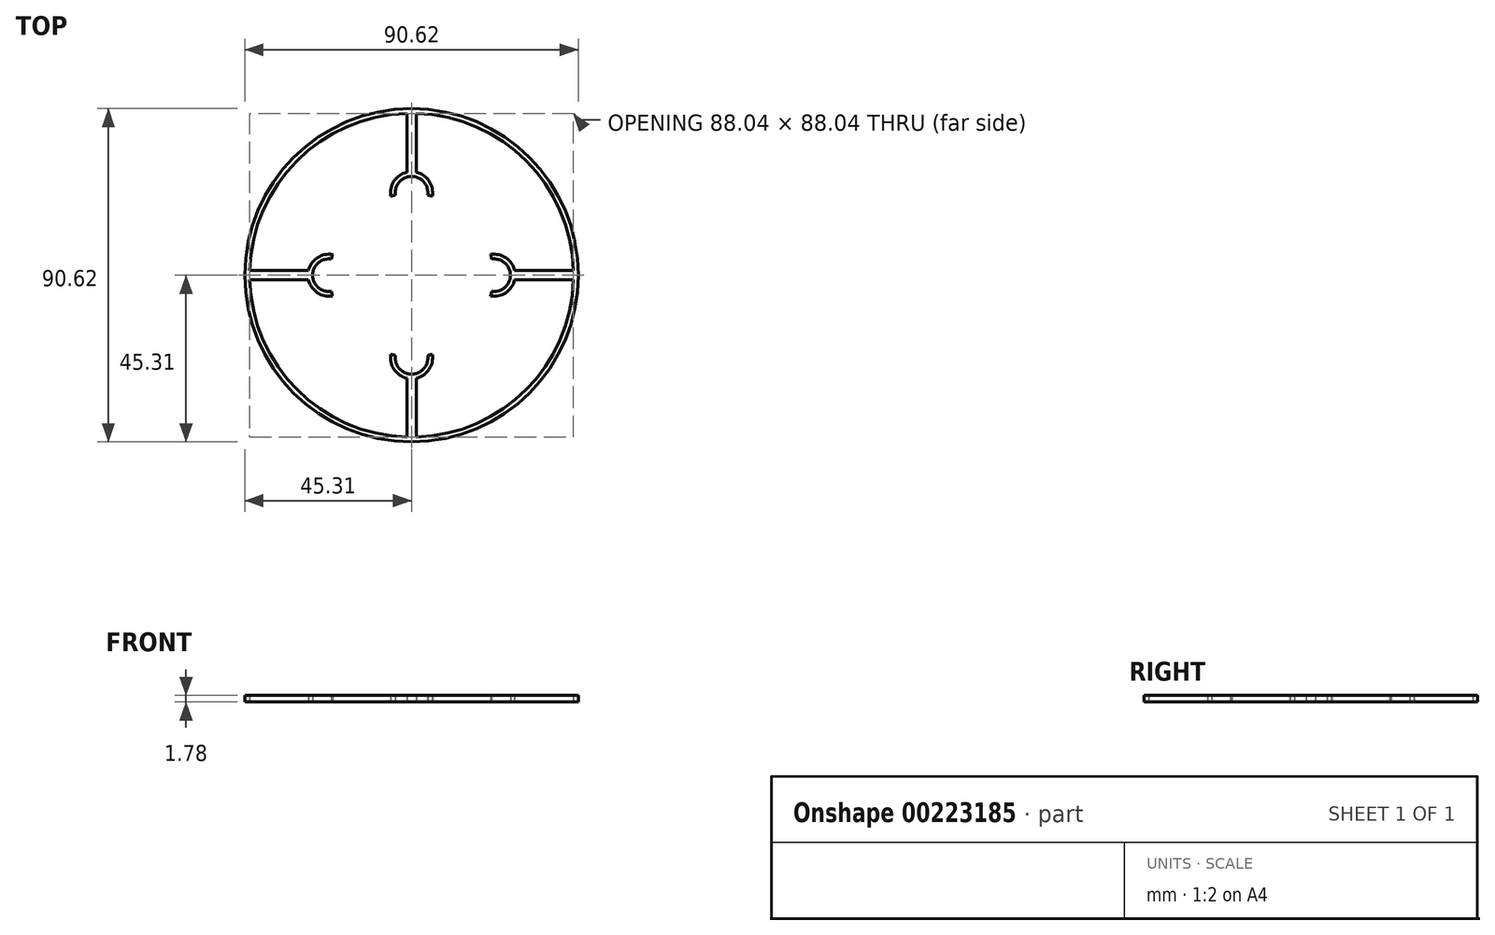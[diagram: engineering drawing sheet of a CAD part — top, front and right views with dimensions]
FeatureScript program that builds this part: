
annotation { "Feature Type Name" : "Feature", "Feature Type Description" : "" }
export const myFeature = defineFeature(function(context is Context, id is Id, definition is map)
    precondition{}
    {
        {
            var Q0;
            Q0=qCreatedBy(makeId("Top.planeOp"),FACE);
            var sketch = newSketch(context, id + "F0", { "sketchPlane" : qUnion([Q0])});
            skCircle(sketch, "E0", {"center": v(0, 22.45) * mm, "radius": 4.45 * mm});
            skCircle(sketch, "E1", {"center": v(22.45, 0) * mm, "radius": 4.45 * mm});
            skCircle(sketch, "E2", {"center": v(0, -22.45) * mm, "radius": 4.45 * mm});
            skCircle(sketch, "E3", {"center": v(-22.45, 0) * mm, "radius": 4.45 * mm});
            skLineSegment(sketch, "E4", {"start": v(0, 22.45) * mm, "end": v(0, 0) * mm, "construction": true});
            skLineSegment(sketch, "E5", {"start": v(0, 0) * mm, "end": v(22.45, 0) * mm, "construction": true});
            skLineSegment(sketch, "E6", {"start": v(-22.45, 0) * mm, "end": v(0, 0) * mm, "construction": true});
            skLineSegment(sketch, "E7", {"start": v(0, 0) * mm, "end": v(0, -22.45) * mm, "construction": true});
            skArc(sketch, "E8.0", {"start": v(-1.27, 28.02) * mm, "mid": v(0, 16.74) * mm, "end": v(1.27, 28.02) * mm});
            skArc(sketch, "E9.0", {"start": v(-28.02, -1.27) * mm, "mid": v(-16.74, 0) * mm, "end": v(-28.02, 1.27) * mm});
            skArc(sketch, "E10.0", {"start": v(28.02, 1.27) * mm, "mid": v(16.74, 0) * mm, "end": v(28.02, -1.27) * mm});
            skArc(sketch, "E11.0", {"start": v(1.27, -28.02) * mm, "mid": v(0, -16.74) * mm, "end": v(-1.27, -28.02) * mm});
            skLineSegment(sketch, "E12", {"start": v(0, 22.45) * mm, "end": v(0, 44.04) * mm, "construction": true});
            skArc(sketch, "E13", {"start": v(-1.27, 44.02) * mm, "mid": v(-31.14, 31.14) * mm, "end": v(-44.02, 1.27) * mm});
            skCircle(sketch, "E14.0", {"center": v(0, 0) * mm, "radius": 45.31 * mm});
            skLineSegment(sketch, "E15.0", {"start": v(-1.27, 28.02) * mm, "end": v(-1.27, 44.02) * mm});
            skLineSegment(sketch, "E16.0", {"start": v(1.27, 28.02) * mm, "end": v(1.27, 44.02) * mm});
            skLineSegment(sketch, "E17.1.0", {"start": v(-28.02, -1.27) * mm, "end": v(-44.02, -1.27) * mm});
            skLineSegment(sketch, "E17.1.1", {"start": v(-28.02, 1.27) * mm, "end": v(-44.02, 1.27) * mm});
            skLineSegment(sketch, "E17.2.0", {"start": v(1.27, -28.02) * mm, "end": v(1.27, -44.02) * mm});
            skLineSegment(sketch, "E17.2.1", {"start": v(-1.27, -28.02) * mm, "end": v(-1.27, -44.02) * mm});
            skLineSegment(sketch, "E18.1.3.0", {"start": v(28.02, 1.27) * mm, "end": v(44.02, 1.27) * mm});
            skLineSegment(sketch, "E18.3.3.0", {"start": v(28.02, -1.27) * mm, "end": v(44.02, -1.27) * mm});
            skPoint(sketch, "E19.orphan", {"position": v(1.27, 41.5) * mm});
            skPoint(sketch, "E20.orphan", {"position": v(-1.27, 41.5) * mm});
            skPoint(sketch, "E21.orphan", {"position": v(-1.27, 22.45) * mm});
            skPoint(sketch, "E22.orphan", {"position": v(1.27, 22.45) * mm});
            skArc(sketch, "E23.trimOffspring", {"start": v(-44.02, -1.27) * mm, "mid": v(-31.14, -31.14) * mm, "end": v(-1.27, -44.02) * mm});
            skPoint(sketch, "E24.orphan", {"position": v(-41.5, 1.27) * mm});
            skPoint(sketch, "E25.orphan", {"position": v(-41.5, -1.27) * mm});
            skPoint(sketch, "E26.orphan", {"position": v(-22.45, 1.27) * mm});
            skPoint(sketch, "E27.orphan", {"position": v(-22.45, -1.27) * mm});
            skPoint(sketch, "E28.orphan", {"position": v(-1.27, -22.45) * mm});
            skPoint(sketch, "E29.orphan", {"position": v(1.27, -22.45) * mm});
            skArc(sketch, "E30.trimOffspring", {"start": v(1.27, -44.02) * mm, "mid": v(31.14, -31.14) * mm, "end": v(44.02, -1.27) * mm});
            skPoint(sketch, "E31.orphan", {"position": v(-1.27, -41.5) * mm});
            skPoint(sketch, "E32.orphan", {"position": v(1.27, -41.5) * mm});
            skArc(sketch, "E33.trimOffspring", {"start": v(44.02, 1.27) * mm, "mid": v(31.14, 31.14) * mm, "end": v(1.27, 44.02) * mm});
            skPoint(sketch, "E34.orphan", {"position": v(41.5, 1.27) * mm});
            skPoint(sketch, "E35.orphan", {"position": v(41.5, -1.27) * mm});
            skPoint(sketch, "E36.orphan", {"position": v(22.45, 1.27) * mm});
            skPoint(sketch, "E37.orphan", {"position": v(22.45, -1.27) * mm});
            skSolve(sketch);
        }
        {
            var Q0;
            Q0=makeQuery(id+"F0.imprint","IMPRINT",FACE,{"disambiguationData":[TD([[makeQuery(id+"F0.imprint","IMPRINT",EDGE,{"derivedFrom":sQuery(id+"F0.wireOp",EDGE,"E0")}),-1.0]])]});
            extrude(context, id + "F1", {"entities" : qUnion([Q0]), "depth" : 1.78 * mm});
        }
        {
            var Q0;
            Q0=qCreatedBy(makeId("Top.planeOp"),FACE);
            var sketch = newSketch(context, id + "F2", { "sketchPlane" : qUnion([Q0])});
            skCircle(sketch, "E38", {"center": v(0, 0) * mm, "radius": 22.23 * mm});
            skSolve(sketch);
        }
        {
            var Q0;
            Q0=makeQuery(id+"F2.imprint","IMPRINT",FACE,{"disambiguationData":[TD([[makeQuery(id+"F2.imprint","IMPRINT",EDGE,{"derivedFrom":sQuery(id+"F2.wireOp",EDGE,"E38")}),1.0]])]});
            extrude(context, id + "F3", {"entities" : qUnion([Q0]), "operationType" : NewBodyOperationType.REMOVE, "depth" : 12.7 * mm});
        }
    });
